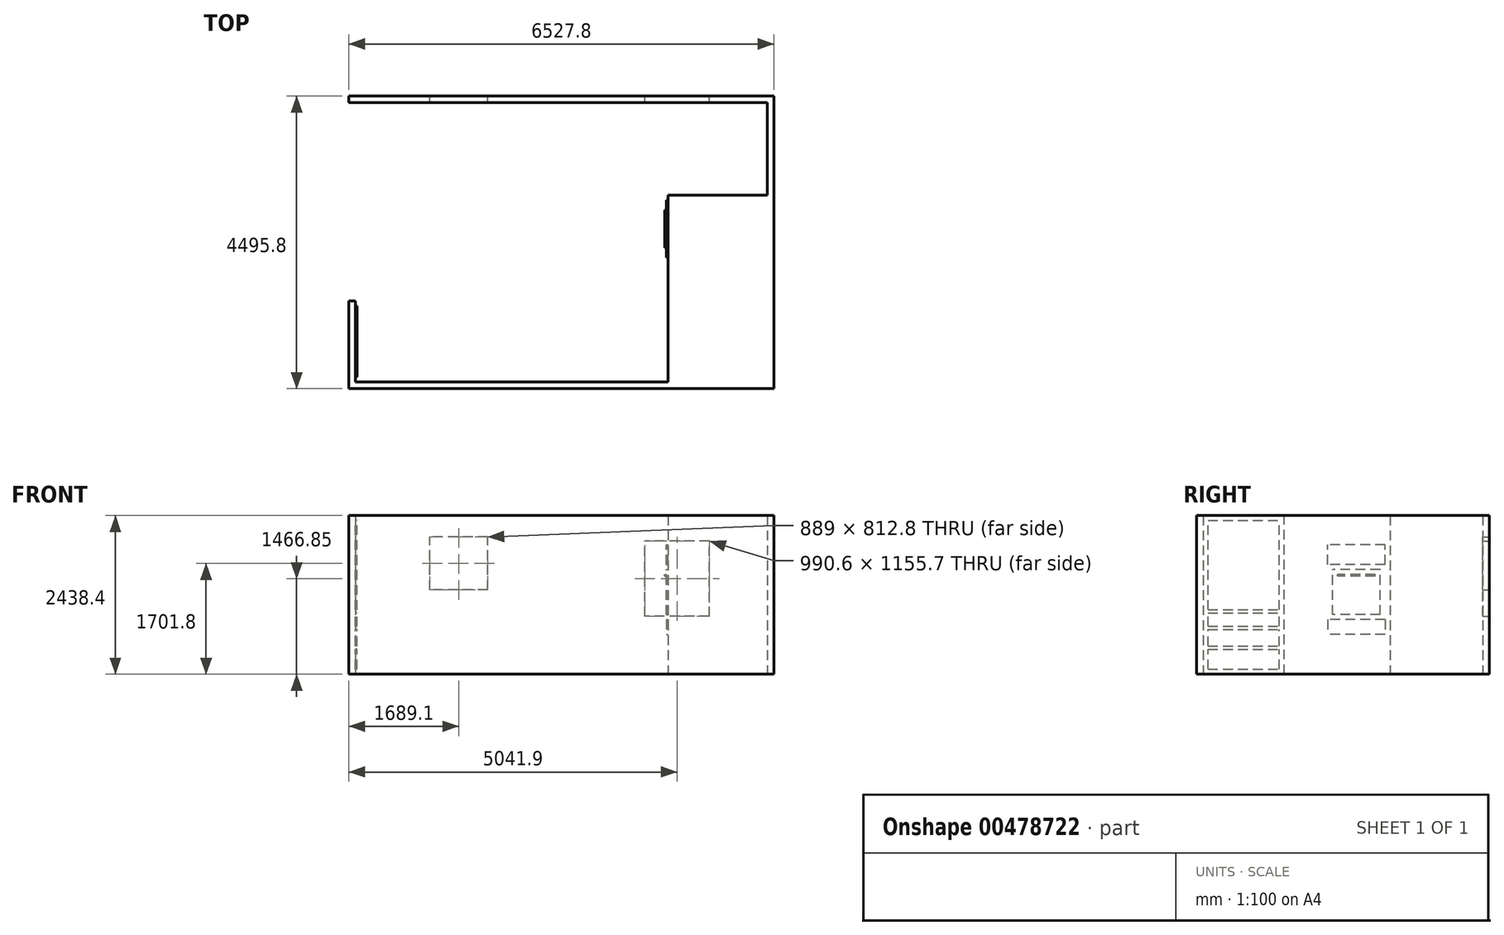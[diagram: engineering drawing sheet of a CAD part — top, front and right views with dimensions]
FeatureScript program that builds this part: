
annotation { "Feature Type Name" : "Feature", "Feature Type Description" : "" }
export const myFeature = defineFeature(function(context is Context, id is Id, definition is map)
    precondition{}
    {
        {
            var Q0;
            Q0=qCreatedBy(makeId("Top.planeOp"),FACE);
            var sketch = newSketch(context, id + "F0", { "sketchPlane" : qUnion([Q0])});
            skLineSegment(sketch, "E0", {"start": v(-7031.1, 1781.65) * mm, "end": v(-503.3, 1781.65) * mm});
            skLineSegment(sketch, "E1", {"start": v(-503.3, 1781.65) * mm, "end": v(-503.3, -2714.15) * mm});
            skLineSegment(sketch, "E2", {"start": v(-503.3, -2714.15) * mm, "end": v(-7031.1, -2714.15) * mm});
            skLineSegment(sketch, "E3", {"start": v(-7031.1, -2714.15) * mm, "end": v(-7031.1, 1781.65) * mm});
            skLineSegment(sketch, "E4", {"start": v(-604.9, 257.65) * mm, "end": v(-2128.9, 257.65) * mm});
            skLineSegment(sketch, "E5", {"start": v(-2128.9, 257.65) * mm, "end": v(-2128.9, -2612.55) * mm});
            skLineSegment(sketch, "E6.bottom", {"start": v(-7031.1, -1063.15) * mm, "end": v(-7640.7, -1063.15) * mm});
            skLineSegment(sketch, "E6.top", {"start": v(-7031.1, -2714.15) * mm, "end": v(-7640.7, -2714.15) * mm});
            skLineSegment(sketch, "E6.left", {"start": v(-7031.1, -1063.15) * mm, "end": v(-7031.1, -2714.15) * mm});
            skLineSegment(sketch, "E6.right", {"start": v(-7640.7, -1063.15) * mm, "end": v(-7640.7, -2714.15) * mm});
            skLineSegment(sketch, "E7.0", {"start": v(-6929.5, 1680.05) * mm, "end": v(-604.9, 1680.05) * mm});
            skLineSegment(sketch, "E7.1", {"start": v(-6929.5, -2612.55) * mm, "end": v(-6929.5, 1680.05) * mm});
            skLineSegment(sketch, "E7.2", {"start": v(-2128.9, -2612.55) * mm, "end": v(-6929.5, -2612.55) * mm});
            skLineSegment(sketch, "E7.3", {"start": v(-604.9, 1680.05) * mm, "end": v(-604.9, 257.65) * mm});
            skLineSegment(sketch, "E8.bottom", {"start": v(-7640.7, -1063.15) * mm, "end": v(-8097.9, -1063.15) * mm});
            skLineSegment(sketch, "E8.top", {"start": v(-7640.7, -2714.15) * mm, "end": v(-8097.9, -2714.15) * mm});
            skLineSegment(sketch, "E8.right", {"start": v(-8097.9, -1063.15) * mm, "end": v(-8097.9, -2714.15) * mm});
            skSolve(sketch);
        }
        {
            var Q0;
            Q0=makeQuery(id+"F0.imprint","IMPRINT",FACE,{"disambiguationData":[TD([[makeQuery(id+"F0.imprint","IMPRINT",EDGE,{"derivedFrom":sQuery(id+"F0.wireOp",EDGE,"E0")}),-1.0]])]});
            var Q1;
            Q1=sQuery(id+"F0.wireOp",EDGE,"E0");
            var Q2;
            Q2=sQuery(id+"F0.wireOp",EDGE,"E3");
            var Q3;
            Q3=sQuery(id+"F0.wireOp",EDGE,"E2");
            var Q4;
            Q4=sQuery(id+"F0.wireOp",EDGE,"E1");
            extrude(context, id + "F1", {"entities" : qUnion([Q0]), "surfaceEntities" : qUnion([Q1, Q2, Q3, Q4]), "depth" : 2438.4 * mm});
        }
        {
            var Q0;
            Q0=makeQuery(id+"F1.opExtrude","SWEPT_FACE",FACE,{"disambiguationData":[OSD([sQuery(id+"F0.wireOp",EDGE,"E0")])]});
            var sketch = newSketch(context, id + "F2", { "sketchPlane" : qUnion([Q0])});
            skLineSegment(sketch, "E9.bottom", {"start": v(1493.9, 889) * mm, "end": v(2484.5, 889) * mm});
            skLineSegment(sketch, "E9.top", {"start": v(1493.9, 2044.7) * mm, "end": v(2484.5, 2044.7) * mm});
            skLineSegment(sketch, "E9.left", {"start": v(1493.9, 889) * mm, "end": v(1493.9, 2044.7) * mm});
            skLineSegment(sketch, "E9.right", {"start": v(2484.5, 889) * mm, "end": v(2484.5, 2044.7) * mm});
            skLineSegment(sketch, "E10.bottom", {"start": v(4897.5, 1295.4) * mm, "end": v(5786.5, 1295.4) * mm});
            skLineSegment(sketch, "E10.top", {"start": v(4897.5, 2108.2) * mm, "end": v(5786.5, 2108.2) * mm});
            skLineSegment(sketch, "E10.left", {"start": v(4897.5, 1295.4) * mm, "end": v(4897.5, 2108.2) * mm});
            skLineSegment(sketch, "E10.right", {"start": v(5786.5, 1295.4) * mm, "end": v(5786.5, 2108.2) * mm});
            skSolve(sketch);
        }
        {
            var Q0;
            Q0 = qSketchRegion(id + "F2", true);
            extrude(context, id + "F3", {"entities" : qUnion([Q0]), "operationType" : NewBodyOperationType.REMOVE, "endBound" : BoundingType.SYMMETRIC, "oppositeDirection" : true, "depth" : 254 * mm});
        }
        {
            var Q0;
            Q0=makeQuery(id+"F1.opExtrude","SWEPT_FACE",FACE,{"disambiguationData":[OSD([sQuery(id+"F0.wireOp",EDGE,"E7.1")])]});
            var sketch = newSketch(context, id + "F4", { "sketchPlane" : qUnion([Q0])});
            skLineSegment(sketch, "E11.bottom", {"start": v(1680.05, 0) * mm, "end": v(-1367.95, 0) * mm});
            skLineSegment(sketch, "E11.top", {"start": v(1680.05, 2438.4) * mm, "end": v(-1367.95, 2438.4) * mm});
            skLineSegment(sketch, "E11.left", {"start": v(1680.05, 0) * mm, "end": v(1680.05, 2438.4) * mm});
            skLineSegment(sketch, "E11.right", {"start": v(-1367.95, 0) * mm, "end": v(-1367.95, 2438.4) * mm});
            skSolve(sketch);
        }
        {
            var Q0;
            Q0 = qSketchRegion(id + "F4", true);
            extrude(context, id + "F5", {"entities" : qUnion([Q0]), "operationType" : NewBodyOperationType.REMOVE, "endBound" : BoundingType.UP_TO_NEXT, "oppositeDirection" : true, "depth" : 25.4 * mm, "offsetDistance" : 25.4 * mm});
        }
        {
            var Q0;
            Q0=makeQuery(id+"F1.opExtrude","SWEPT_FACE",FACE,{"disambiguationData":[OSD([sQuery(id+"F0.wireOp",EDGE,"E5")])]});
            var sketch = newSketch(context, id + "F6", { "sketchPlane" : qUnion([Q0])});
            skLineSegment(sketch, "E12.bottom", {"start": v(-105.25, 914.4) * mm, "end": v(621.83, 914.4) * mm});
            skLineSegment(sketch, "E12.top", {"start": v(-105.25, 1608.15) * mm, "end": v(621.83, 1608.15) * mm});
            skLineSegment(sketch, "E12.left", {"start": v(-105.25, 914.4) * mm, "end": v(-105.25, 1608.15) * mm});
            skLineSegment(sketch, "E12.right", {"start": v(621.83, 914.4) * mm, "end": v(621.83, 1608.15) * mm});
            skSolve(sketch);
        }
        {
            var Q0;
            Q0 = qSketchRegion(id + "F6", true);
            extrude(context, id + "F7", {"entities" : qUnion([Q0]), "operationType" : NewBodyOperationType.ADD, "depth" : 25.4 * mm, "offsetDistance" : 25.4 * mm});
        }
        {
            var Q0;
            Q0=makeQuery(id+"F7.opExtrude","CAP_FACE",FACE,{"disambiguationData":[OSD([sQuery(id+"F6.wireOp",EDGE,"E12.bottom"),sQuery(id+"F6.wireOp",EDGE,"E12.top"),sQuery(id+"F6.wireOp",EDGE,"E12.left"),sQuery(id+"F6.wireOp",EDGE,"E12.right")])],"isStart":false});
            var sketch = newSketch(context, id + "F8", { "sketchPlane" : qUnion([Q0])});
            skLineSegment(sketch, "E13.bottom", {"start": v(-29.05, 1506.55) * mm, "end": v(545.63, 1506.55) * mm});
            skLineSegment(sketch, "E13.top", {"start": v(-29.05, 1531.95) * mm, "end": v(545.63, 1531.95) * mm});
            skLineSegment(sketch, "E13.left", {"start": v(-29.05, 1506.55) * mm, "end": v(-29.05, 1531.95) * mm});
            skLineSegment(sketch, "E13.right", {"start": v(545.63, 1506.55) * mm, "end": v(545.63, 1531.95) * mm});
            skSolve(sketch);
        }
        {
            var Q0;
            Q0 = qSketchRegion(id + "F8", true);
            extrude(context, id + "F9", {"entities" : qUnion([Q0]), "operationType" : NewBodyOperationType.ADD, "depth" : 25.4 * mm, "offsetDistance" : 25.4 * mm});
        }
        {
            var Q0;
            Q0=makeQuery(id+"F1.opExtrude","SWEPT_FACE",FACE,{"disambiguationData":[OSD([sQuery(id+"F0.wireOp",EDGE,"E5")])]});
            var sketch = newSketch(context, id + "F10", { "sketchPlane" : qUnion([Q0])});
            skLineSegment(sketch, "E14.bottom", {"start": v(-181.45, 1684.35) * mm, "end": v(698.03, 1684.35) * mm});
            skLineSegment(sketch, "E14.top", {"start": v(-181.45, 1989.15) * mm, "end": v(698.03, 1989.15) * mm});
            skLineSegment(sketch, "E14.left", {"start": v(-181.45, 1684.35) * mm, "end": v(-181.45, 1989.15) * mm});
            skLineSegment(sketch, "E14.right", {"start": v(698.03, 1684.35) * mm, "end": v(698.03, 1989.15) * mm});
            skLineSegment(sketch, "E15.bottom", {"start": v(-181.45, 609.6) * mm, "end": v(698.03, 609.6) * mm});
            skLineSegment(sketch, "E15.top", {"start": v(-181.45, 838.2) * mm, "end": v(698.03, 838.2) * mm});
            skLineSegment(sketch, "E15.left", {"start": v(-181.45, 838.2) * mm, "end": v(-181.45, 609.6) * mm});
            skLineSegment(sketch, "E15.right", {"start": v(698.03, 838.2) * mm, "end": v(698.03, 609.6) * mm});
            skSolve(sketch);
        }
        {
            var Q0;
            Q0 = qSketchRegion(id + "F10", true);
            extrude(context, id + "F11", {"entities" : qUnion([Q0]), "operationType" : NewBodyOperationType.ADD, "depth" : 25.4 * mm, "offsetDistance" : 25.4 * mm});
        }
        {
            var Q0;
            Q0=makeQuery(id+"F1.opExtrude","SWEPT_FACE",FACE,{"disambiguationData":[OSD([sQuery(id+"F0.wireOp",EDGE,"E7.1")])]});
            var sketch = newSketch(context, id + "F12", { "sketchPlane" : qUnion([Q0])});
            skLineSegment(sketch, "E16.bottom", {"start": v(-2536.35, 76.2) * mm, "end": v(-1444.15, 76.2) * mm});
            skLineSegment(sketch, "E16.top", {"start": v(-2536.35, 381) * mm, "end": v(-1444.15, 381) * mm});
            skLineSegment(sketch, "E16.left", {"start": v(-2536.35, 76.2) * mm, "end": v(-2536.35, 381) * mm});
            skLineSegment(sketch, "E16.right", {"start": v(-1444.15, 76.2) * mm, "end": v(-1444.15, 381) * mm});
            skLineSegment(sketch, "E17.bottom", {"start": v(-2536.35, 431.8) * mm, "end": v(-1444.15, 431.8) * mm});
            skLineSegment(sketch, "E17.top", {"start": v(-2536.35, 685.8) * mm, "end": v(-1444.15, 685.8) * mm});
            skLineSegment(sketch, "E17.left", {"start": v(-2536.35, 431.8) * mm, "end": v(-2536.35, 685.8) * mm});
            skLineSegment(sketch, "E17.right", {"start": v(-1444.15, 431.8) * mm, "end": v(-1444.15, 685.8) * mm});
            skLineSegment(sketch, "E18.bottom", {"start": v(-2536.35, 736.6) * mm, "end": v(-1444.15, 736.6) * mm});
            skLineSegment(sketch, "E18.top", {"start": v(-2536.35, 939.8) * mm, "end": v(-1444.15, 939.8) * mm});
            skLineSegment(sketch, "E18.left", {"start": v(-2536.35, 736.6) * mm, "end": v(-2536.35, 939.8) * mm});
            skLineSegment(sketch, "E18.right", {"start": v(-1444.15, 736.6) * mm, "end": v(-1444.15, 939.8) * mm});
            skPoint(sketch, "E19.firstSnap0", {"position": v(-2536.35, 838.2) * mm});
            skLineSegment(sketch, "E19.bottom", {"start": v(-2536.35, 990.6) * mm, "end": v(-1444.15, 990.6) * mm});
            skLineSegment(sketch, "E19.top", {"start": v(-2536.35, 2362.2) * mm, "end": v(-1444.15, 2362.2) * mm});
            skLineSegment(sketch, "E19.left", {"start": v(-2536.35, 990.6) * mm, "end": v(-2536.35, 2362.2) * mm});
            skLineSegment(sketch, "E19.right", {"start": v(-1444.15, 990.6) * mm, "end": v(-1444.15, 2362.2) * mm});
            skLineSegment(sketch, "E20", {"start": v(-1444.15, 2362.2) * mm, "end": v(-1444.15, 0) * mm, "construction": true});
            skSolve(sketch);
        }
        {
            var Q0;
            Q0 = qSketchRegion(id + "F12", true);
            extrude(context, id + "F13", {"entities" : qUnion([Q0]), "operationType" : NewBodyOperationType.ADD, "depth" : 25.4 * mm, "offsetDistance" : 25.4 * mm});
        }
    });
